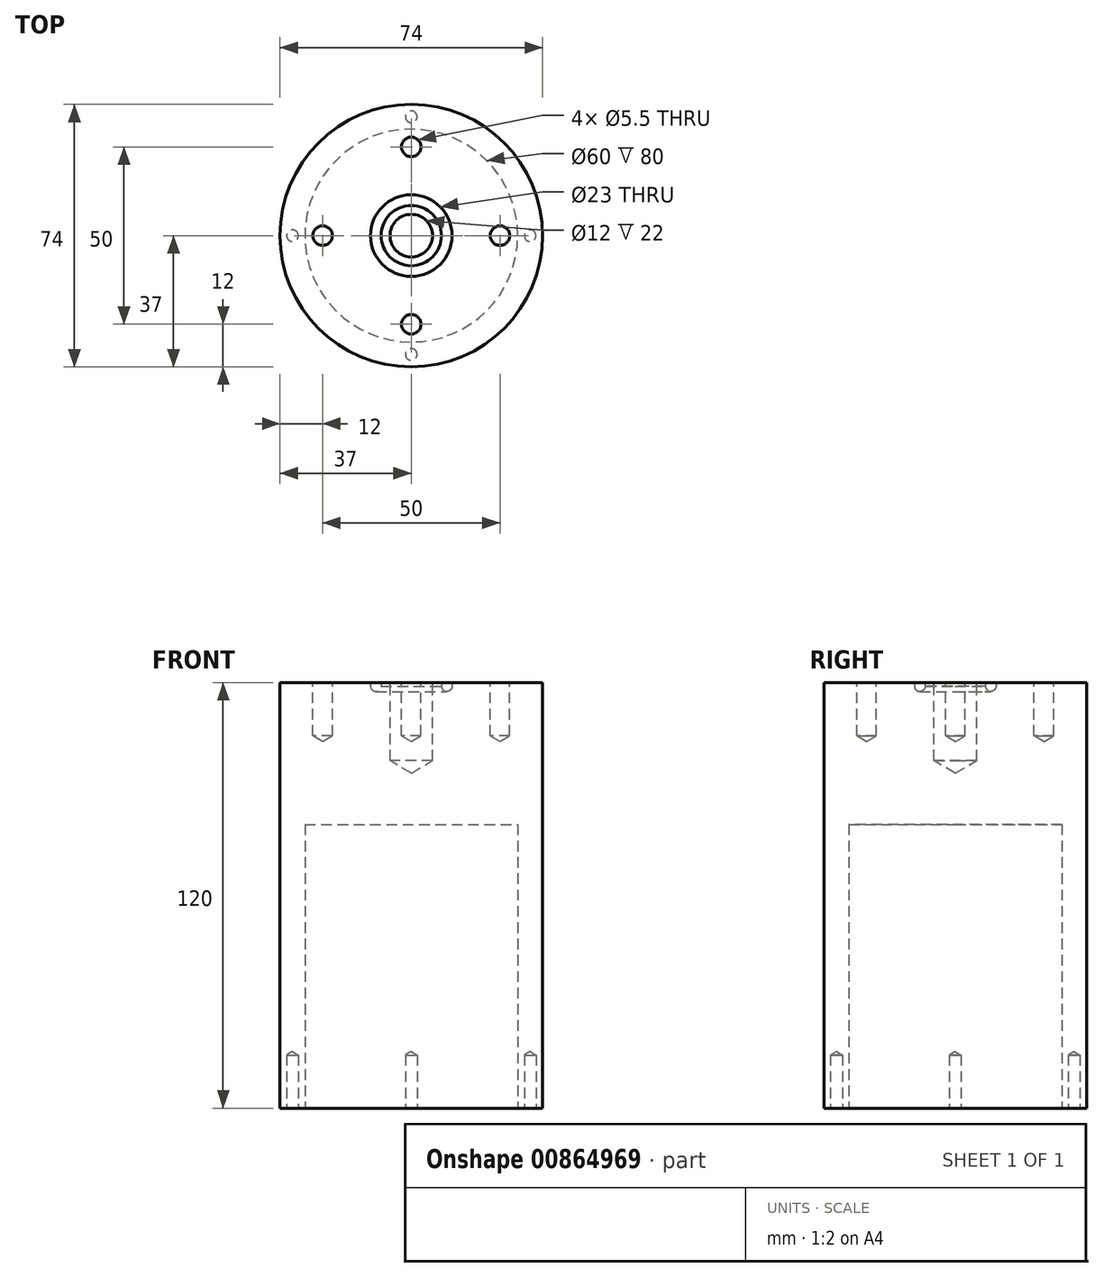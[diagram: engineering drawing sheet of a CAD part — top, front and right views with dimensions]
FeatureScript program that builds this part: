
annotation { "Feature Type Name" : "Feature", "Feature Type Description" : "" }
export const myFeature = defineFeature(function(context is Context, id is Id, definition is map)
    precondition{}
    {
        {
            var Q0;
            Q0=qCreatedBy(makeId("Top.planeOp"),FACE);
            var sketch = newSketch(context, id + "F0", { "sketchPlane" : qUnion([Q0])});
            skCircle(sketch, "E0", {"center": v(0, 0) * mm, "radius": 37 * mm});
            skSolve(sketch);
        }
        {
            var Q0;
            Q0=makeQuery(id+"F0.imprint","IMPRINT",FACE,{"disambiguationData":[TD([[makeQuery(id+"F0.imprint","IMPRINT",EDGE,{"derivedFrom":sQuery(id+"F0.wireOp",EDGE,"E0")}),1.0]])]});
            extrude(context, id + "F1", {"entities" : qUnion([Q0]), "depth" : 120 * mm, "offsetDistance" : 25 * mm});
        }
        {
            var Q0;
            Q0=makeQuery(id+"F1.opExtrude","CAP_FACE",FACE,{"disambiguationData":[OSD([sQuery(id+"F0.wireOp",EDGE,"E0")])],"isStart":true});
            var sketch = newSketch(context, id + "F2", { "sketchPlane" : qUnion([Q0])});
            skCircle(sketch, "E1", {"center": v(0, 0) * mm, "radius": 30 * mm});
            skSolve(sketch);
        }
        {
            var Q0;
            Q0=makeQuery(id+"F2.imprint","IMPRINT",FACE,{"disambiguationData":[TD([[makeQuery(id+"F2.imprint","IMPRINT",EDGE,{"derivedFrom":sQuery(id+"F2.wireOp",EDGE,"E1")}),1.0]])]});
            extrude(context, id + "F3", {"entities" : qUnion([Q0]), "operationType" : NewBodyOperationType.REMOVE, "oppositeDirection" : true, "depth" : 80 * mm, "offsetDistance" : 25 * mm});
        }
        {
            var Q0;
            Q0=makeQuery(id+"F1.opExtrude","CAP_FACE",FACE,{"disambiguationData":[OSD([sQuery(id+"F0.wireOp",EDGE,"E0")])],"isStart":false});
            var sketch = newSketch(context, id + "F4", { "sketchPlane" : qUnion([Q0])});
            skCircle(sketch, "E2", {"center": v(0, 0) * mm, "radius": 10 * mm});
            skSolve(sketch);
        }
        {
            var Q0;
            Q0=sQuery(id+"F4.wireOp",VERTEX,"E2.center");
            var Q1;
            Q1=makeQuery(id+"F1.opExtrude","SWEPT_BODY",BODY,{"disambiguationData":[OSD([sQuery(id+"F0.wireOp",EDGE,"E0")])]});
            hole(context, id + "F5", {"style" : HoleStyle.SIMPLE, "endStyle" : HoleEndStyle.BLIND, "holeDiameter" : 12 * mm, "majorDiameter" : 5 * mm, "holeDepth" : 22 * mm, "isTappedThrough" : true, "tappedDepth" : 12 * mm, "tapClearance" : 3, "locations" : qUnion([Q0]), "scope" : qUnion([Q1])});
        }
        {
            var Q0;
            Q0=qCreatedBy(makeId("Front.planeOp"),FACE);
            var sketch = newSketch(context, id + "F6", { "sketchPlane" : qUnion([Q0])});
            skLineSegment(sketch, "E3.0", {"start": v(-37, 120) * mm, "end": v(37, 120) * mm});
            skArc(sketch, "E4", {"start": v(-11.5, 118.98) * mm, "mid": v(-9.99, 117.48) * mm, "end": v(-8.5, 119) * mm});
            skLineSegment(sketch, "E5.top", {"start": v(-8.5, 120) * mm, "end": v(-11.5, 120) * mm});
            skLineSegment(sketch, "E5.left", {"start": v(-8.5, 119) * mm, "end": v(-8.5, 120) * mm});
            skLineSegment(sketch, "E5.right", {"start": v(-11.5, 118.98) * mm, "end": v(-11.5, 120) * mm});
            skPoint(sketch, "E6.0", {"position": v(0, 0) * mm});
            skLineSegment(sketch, "E7", {"start": v(0, 127.44) * mm, "end": v(0, -17.2) * mm});
            skSolve(sketch);
        }
        {
            var Q0;
            Q0 = qSketchRegion(id + "F6", true);
            var Q1;
            Q1=sQuery(id+"F6.wireOp",EDGE,"E7");
            revolve(context, id + "F7", {"operationType" : NewBodyOperationType.REMOVE, "surfaceOperationType" : NewSurfaceOperationType.NEW, "entities" : qUnion([Q0]), "axis" : qUnion([Q1]), "revolveType" : RevolveType.FULL, "oppositeDirection" : true});
        }
        {
            var Q0;
            {var subQ0=sQuery(id+"F0.wireOp",EDGE,"E0");Q0=makeQuery(id+"F7.boolean.opBoolean","SPLIT",FACE,{"disambiguationData":[TD([makeQuery(id+"F1.opExtrude","SWEPT_FACE",FACE,{"disambiguationData":[OSD([subQ0])]})])],"derivedFrom":makeQuery(id+"F1.opExtrude","CAP_FACE",FACE,{"disambiguationData":[OSD([subQ0])],"isStart":false})});}
            var sketch = newSketch(context, id + "F8", { "sketchPlane" : qUnion([Q0])});
            skCircle(sketch, "E8", {"center": v(0, 0) * mm, "radius": 25 * mm});
            skPoint(sketch, "E9", {"position": v(-25, 0) * mm});
            skPoint(sketch, "E10", {"position": v(0, 25) * mm});
            skPoint(sketch, "E11", {"position": v(25, 0) * mm});
            skPoint(sketch, "E12", {"position": v(0, -25) * mm});
            skSolve(sketch);
        }
        {
            var Q0;
            Q0=sQuery(id+"F8.wireOp",VERTEX,"E9");
            var Q1;
            Q1=sQuery(id+"F8.wireOp",VERTEX,"E10");
            var Q2;
            Q2=sQuery(id+"F8.wireOp",VERTEX,"E11");
            var Q3;
            Q3=sQuery(id+"F8.wireOp",VERTEX,"E12");
            var Q4;
            Q4=makeQuery(id+"F1.opExtrude","SWEPT_BODY",BODY,{"disambiguationData":[OSD([sQuery(id+"F0.wireOp",EDGE,"E0")])]});
            hole(context, id + "F9", {"style" : HoleStyle.SIMPLE, "endStyle" : HoleEndStyle.BLIND, "standardTappedOrClearance" : lookupTablePath({ "fit" : "Normal", "standard" : "ISO", "size" : "M5", "type" : "Clearance" }), "standardBlindInLast" : lookupTablePath({ "fit" : "Standard", "standard" : "ISO", "size" : "M5", "type" : "Clearance" }), "holeDiameter" : 5.5 * mm, "majorDiameter" : 5 * mm, "holeDepth" : 15 * mm, "isTappedThrough" : true, "tappedDepth" : 12 * mm, "tapClearance" : 3, "locations" : qUnion([Q0, Q1, Q2, Q3]), "scope" : qUnion([Q4])});
        }
        {
            var Q0;
            Q0=makeQuery(id+"F1.opExtrude","CAP_FACE",FACE,{"disambiguationData":[OSD([sQuery(id+"F0.wireOp",EDGE,"E0")])],"isStart":true});
            var sketch = newSketch(context, id + "F10", { "sketchPlane" : qUnion([Q0])});
            skCircle(sketch, "E13", {"center": v(0, 0) * mm, "radius": 33.5 * mm});
            skPoint(sketch, "E14", {"position": v(-33.5, 0) * mm});
            skPoint(sketch, "E15", {"position": v(0, 33.5) * mm});
            skPoint(sketch, "E16", {"position": v(33.5, 0) * mm});
            skPoint(sketch, "E17", {"position": v(0, -33.5) * mm});
            skSolve(sketch);
        }
        {
            var Q0;
            Q0=sQuery(id+"F10.wireOp",VERTEX,"E14");
            var Q1;
            Q1=sQuery(id+"F10.wireOp",VERTEX,"E15");
            var Q2;
            Q2=sQuery(id+"F10.wireOp",VERTEX,"E16");
            var Q3;
            Q3=sQuery(id+"F10.wireOp",VERTEX,"E17");
            var Q4;
            Q4=makeQuery(id+"F1.opExtrude","SWEPT_BODY",BODY,{"disambiguationData":[OSD([sQuery(id+"F0.wireOp",EDGE,"E0")])]});
            hole(context, id + "F11", {"style" : HoleStyle.SIMPLE, "endStyle" : HoleEndStyle.BLIND, "standardTappedOrClearance" : lookupTablePath({ "fit" : "Normal", "standard" : "ISO", "size" : "M3", "type" : "Clearance" }), "standardBlindInLast" : lookupTablePath({ "fit" : "Standard", "standard" : "ISO", "size" : "M3", "type" : "Clearance" }), "holeDiameter" : 3.3 * mm, "majorDiameter" : 5 * mm, "holeDepth" : 15 * mm, "isTappedThrough" : true, "tappedDepth" : 12 * mm, "tapClearance" : 3, "locations" : qUnion([Q0, Q1, Q2, Q3]), "scope" : qUnion([Q4])});
        }
    });
